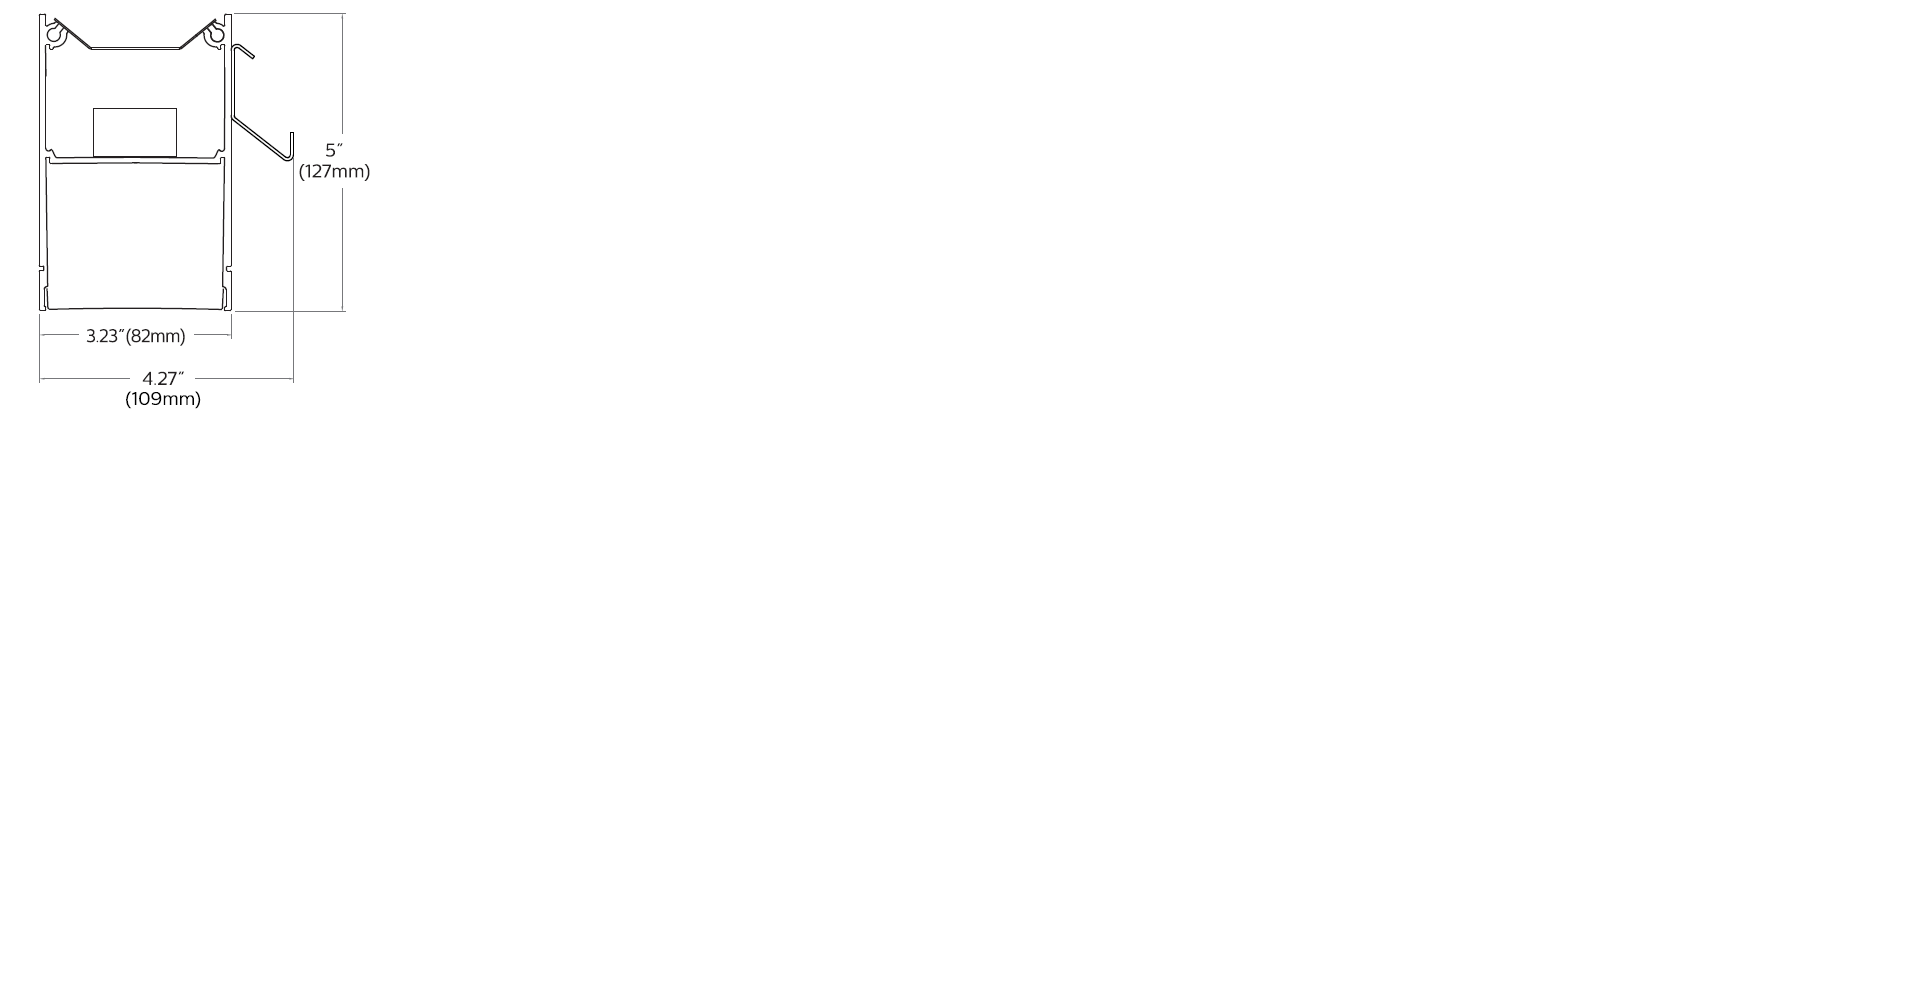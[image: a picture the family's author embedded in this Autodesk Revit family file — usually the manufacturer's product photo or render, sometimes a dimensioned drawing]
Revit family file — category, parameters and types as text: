
# Revit family: Lighting-Wall-Philips_Ledalite-TruGroove_LED
name_source: partatom
category: Lighting Fixtures
revit_build: Autodesk Revit 2017 (Build: 20160720_1515(x64)
units: mm (PartAtom-declared; Revit-internal decimal feet)

## family parameters
Cut with Voids When Loaded = No
Host = Face
Light Source = Yes
OmniClass Number = 23.80.70.11.14
OmniClass Title = General Luminaries, Directional
Part Type = Normal
Room Calculation Point = No
Round Connector Dimension = Use Diameter
Shared = No

## types (33) — shared parameters
Assembly Code = D5020200
Color Filter = 16777215
Default Elevation = 48"
Depth = 5"
Dimming Lamp Color Temperature Shift = <None>
Emit Shape Visible in Rendering = No
Emit from Rectangle Length = 48"
Emit from Rectangle Width = 3 7/32"
End Cap Depth = 3/16"
Housing Material Finish = Powder Coat-Signify-Titanium
Lamp = LED
Last Updated = 6/18/2015
Length = 48"
Lens Material Finish = Acrylic-Signify-White, Translucent
Manufacturer = Ledalite
Photometry Comments = Candela values are absolute.
Product Family = TruGroove Wall LED
Product Page URL = http://www.lightingproducts.philips.com
Tilt Angle = -90.00°
URL = https://www.signify.com
Voltage = 120 V
Width = 3 7/32"
eCatalog URL = www.ledalite.com

## per-type parameters (varying)
| type | Apparent Load | Description | Photometric Web File |
| 29x1LAEWN | 36 VA | TruGroove Wall Direct, LED, 4000K, 3200 Nominal Delivered Lumens, Asymmetric MesoOptics | 29x1LAEWN.ies |
| 29x1LAGWN | 24 VA | TruGroove Wall Direct, LED, 4000K, 2300 Nominal Delivered Lumens, Asymmetric MesoOptics | 29x1LAGWN.ies |
| 29x1LAKWN | 15 VA | TruGroove Wall Direct, LED, 4000K, 1500 Nominal Delivered Lumens, Asymmetric MesoOptics | 29x1LAKWN.ies |
| 29x1LBEWN | 35 VA | TruGroove Wall Direct, LED, 3500K, 3200 Nominal Delivered Lumens, Asymmetric MesoOptics | 29x1LBEWN.ies |
| 29x1LBGWN | 24 VA | TruGroove Wall Direct, LED, 3500K, 2300 Nominal Delivered Lumens, Asymmetric MesoOptics | 29x1LBGWN.ies |
| 29x1LBKWN | 15 VA | TruGroove Wall Direct, LED, 3500K, 1500 Nominal Delivered Lumens, Asymmetric MesoOptics | 29x1LBKWN.ies |
| 29x1LCEWN | 35 VA | TruGroove Wall Direct, LED, 3000K, 3200 Nominal Delivered Lumens, Asymmetric MesoOptics | 29x1LCEWN.ies |
| 29x1LCGWN | 24 VA | TruGroove Wall Direct, LED, 3000K, 2300 Nominal Delivered Lumens, Asymmetric MesoOptics | 29x1LCGWN.ies |
| 29x1LCKWN | 15 VA | TruGroove Wall Direct, LED, 3000K, 1500 Nominal Delivered Lumens, Asymmetric MesoOptics | 29x1LCKWN.ies |
| 29x3LACNW | 41 VA | TruGroove Wall Indirect, LED, 4000K, 4800 Nominal Delivered Lumens, Asymmetric MesoOptics | 29x3LACNW.ies |
| 29x3LAENW | 29 VA | TruGroove Wall Indirect, LED, 4000K, 3200 Nominal Delivered Lumens, Asymmetric MesoOptics | 29x3LAENW.ies |
| 29x3LBCNW | 41 VA | TruGroove Wall Indirect, LED, 3500K, 4800 Nominal Delivered Lumens, Asymmetric MesoOptics | 29x3LBCNW.ies |
| 29x3LBENW | 29 VA | TruGroove Wall Indirect, LED, 3500K, 3200 Nominal Delivered Lumens, Asymmetric MesoOptics | 29x3LBENW.ies |
| 29x3LCCNW | 41 VA | TruGroove Wall Indirect, LED, 3000K, 4800 Nominal Delivered Lumens, Asymmetric MesoOptics | 29x3LCCNW.ies |
| 29x3LCENW | 26 VA | TruGroove Wall Indirect, LED, 3000K, 3200 Nominal Delivered Lumens, Asymmetric MesoOptics | 29x3LCENW.ies |
| 29x5LABWW | 47 VA | TruGroove Wall Indirect/Direct, LED, 4000K, 5200 Nominal Delivered Lumens, Asymmetric MesoOptics Top and Bottom | 29x5LABWW.ies |
| 29x5LACWW | 41 VA | TruGroove Wall Indirect/Direct, LED, 4000K, 4600 Nominal Delivered Lumens, Asymmetric MesoOptics Top and Bottom | 29x5LACWW.ies |
| 29x5LADWW | 29 VA | TruGroove Wall Indirect/Direct, LED, 4000K, 3500 Nominal Delivered Lumens, Asymmetric MesoOptics Top and Bottom | 29x5LADWW.ies |
| 29x5LBBWW | 46 VA | TruGroove Wall Indirect/Direct, LED, 3500K, 5200 Nominal Delivered Lumens, Asymmetric MesoOptics Top and Bottom | 29x5LBBWW.ies |
| 29x5LBCWW | 41 VA | TruGroove Wall Indirect/Direct, LED, 3500K, 4600 Nominal Delivered Lumens, Asymmetric MesoOptics Top and Bottom | 29x5LBCWW.ies |
| 29x5LBDWW | 29 VA | TruGroove Wall Indirect/Direct, LED, 3500K, 3500 Nominal Delivered Lumens, Asymmetric MesoOptics Top and Bottom | 29x5LBDWW.ies |
| 29x5LCBWW | 46 VA | TruGroove Wall Indirect/Direct, LED, 3000K, 5200 Nominal Delivered Lumens, Asymmetric MesoOptics Top and Bottom | 29x5LCBWW.ies |
| 29x5LCCWW | 41 VA | TruGroove Wall Indirect/Direct, LED, 3000K, 4600 Nominal Delivered Lumens, Asymmetric MesoOptics Top and Bottom | 29x5LCCWW.ies |
| 29x5LCDWW | 29 VA | TruGroove Wall Indirect/Direct, LED, 3000K, 3500 Nominal Delivered Lumens, Asymmetric MesoOptics Top and Bottom | 29x5LCDWW.ies |
| 29x6LABWW | 51 VA | TruGroove Wall Direct/Indirect, LED, 4000K, 5200 Nominal Delivered Lumens, Asymmetirc MesoOptics Top and Bottom | 29x6LABWW.ies |
| 29x6LACWW | 46 VA | TruGroove Wall Direct/Indirect, LED, 4000K, 4600 Nominal Delivered Lumens, Asymmetirc MesoOptics Top and Bottom | 29x6LACWW.ies |
| 29x6LADWW | 35 VA | TruGroove Wall Direct/Indirect, LED, 4000K, 3500 Nominal Delivered Lumens, Asymmetirc MesoOptics Top and Bottom | 29x6LADWW.ies |
| 29x6LBBWW | 50 VA | TruGroove Wall Direct/Indirect, LED, 3500K, 5200 Nominal Delivered Lumens, Asymmetirc MesoOptics Top and Bottom | 29x6LBBWW.ies |
| 29x6LBCWW | 46 VA | TruGroove Wall Direct/Indirect, LED, 3500K, 4600 Nominal Delivered Lumens, Asymmetirc MesoOptics Top and Bottom | 29x6LBCWW.ies |
| 29x6LBDWW | 35 VA | TruGroove Wall Direct/Indirect, LED, 3500K, 3500 Nominal Delivered Lumens, Asymmetirc MesoOptics Top and Bottom | 29x6LBDWW.ies |
| 29x6LCBWW | 50 VA | TruGroove Wall Direct/Indirect, LED, 3000K, 5200 Nominal Delivered Lumens, Asymmetirc MesoOptics Top and Bottom | 29x6LCBWW.ies |
| 29x6LCCWW | 46 VA | TruGroove Wall Direct/Indirect, LED, 3000K, 4600 Nominal Delivered Lumens, Asymmetirc MesoOptics Top and Bottom | 29x6LCCWW.ies |
| 29x6LCDWW | 35 VA | TruGroove Wall Direct/Indirect, LED, 3000K, 3500 Nominal Delivered Lumens, Asymmetirc MesoOptics Top and Bottom | 29x6LCDWW.ies |

note: column(s) folded — value = type name in every type: Catalog Number, Model

## geometry (parser evidence)
native form markers: Blend x6, Sweep x3
no freeform markers — native parametric forms only
